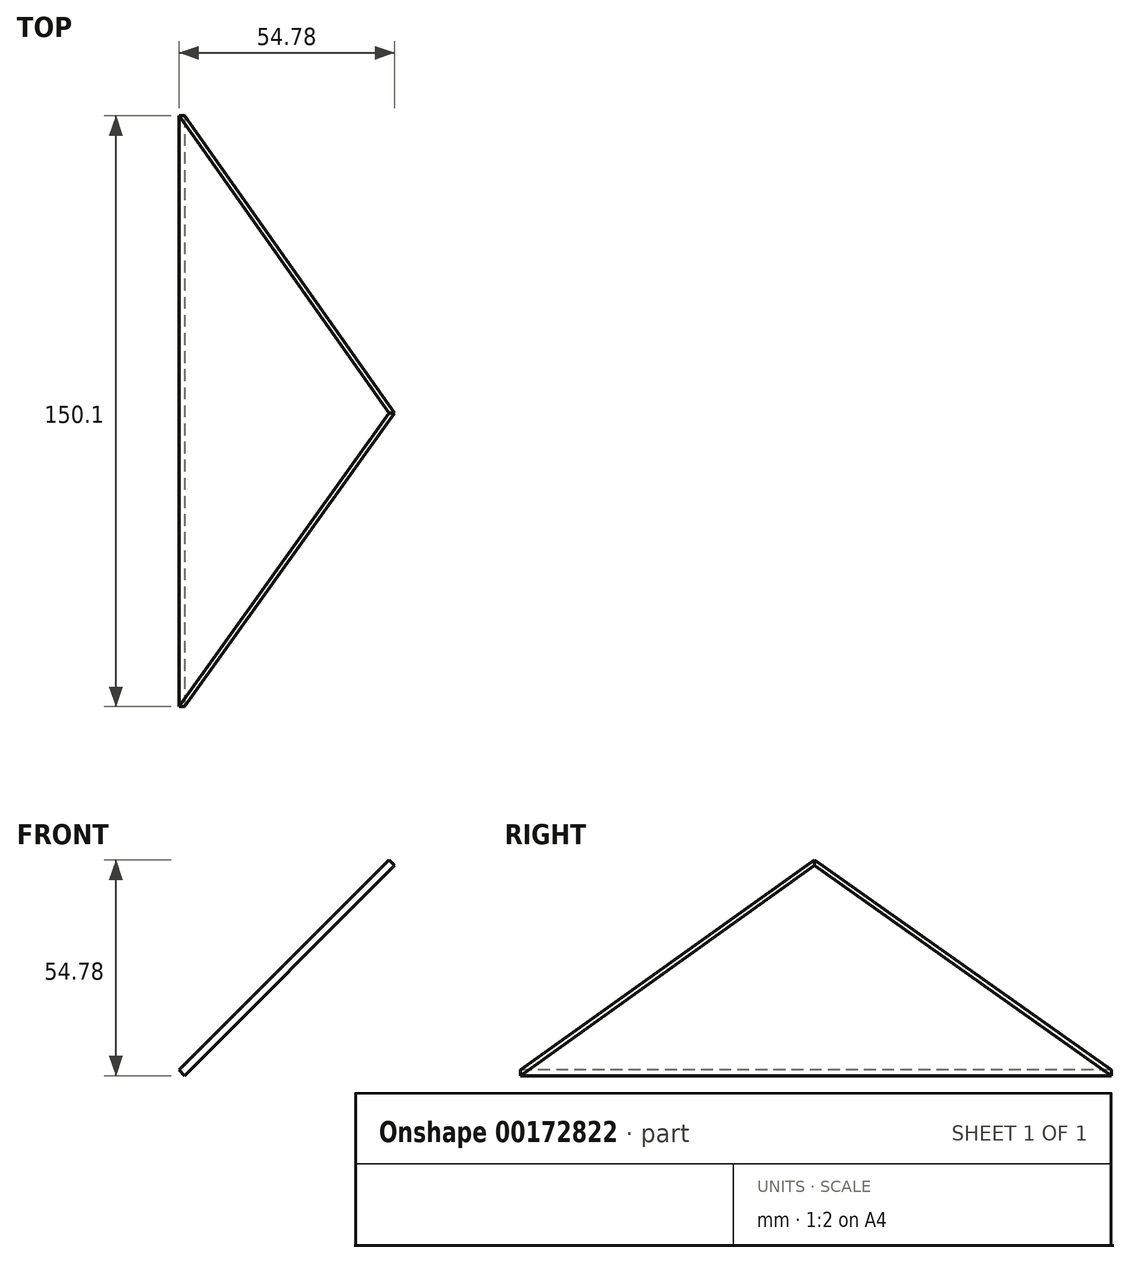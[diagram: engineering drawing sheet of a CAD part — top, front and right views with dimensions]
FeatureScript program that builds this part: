
annotation { "Feature Type Name" : "Feature", "Feature Type Description" : "" }
export const myFeature = defineFeature(function(context is Context, id is Id, definition is map)
    precondition{}
    {
        {
            var Q0;
            Q0=qCreatedBy(makeId("Top.planeOp"),FACE);
            var sketch = newSketch(context, id + "F0", { "sketchPlane" : qUnion([Q0])});
            skLineSegment(sketch, "E0.bottom", {"start": v(-75.48, 75.47) * mm, "end": v(75.05, 75.47) * mm});
            skLineSegment(sketch, "E0.top", {"start": v(-75.48, -74.63) * mm, "end": v(75.05, -74.63) * mm});
            skLineSegment(sketch, "E0.left", {"start": v(-75.48, 75.47) * mm, "end": v(-75.48, -74.63) * mm});
            skLineSegment(sketch, "E0.right", {"start": v(75.05, 75.47) * mm, "end": v(75.05, -74.63) * mm});
            skLineSegment(sketch, "E1", {"start": v(-75.48, -74.63) * mm, "end": v(0, 0) * mm});
            skLineSegment(sketch, "E2", {"start": v(0, 0) * mm, "end": v(75.05, 75.47) * mm});
            skLineSegment(sketch, "E3", {"start": v(-75.48, 75.47) * mm, "end": v(0, 0) * mm});
            skLineSegment(sketch, "E4", {"start": v(75.05, -74.63) * mm, "end": v(0, 0) * mm});
            skSolve(sketch);
        }
        {
            var Q0;
            Q0=qCreatedBy(makeId("Front.planeOp"),FACE);
            var sketch = newSketch(context, id + "F1", { "sketchPlane" : qUnion([Q0])});
            skPoint(sketch, "E5", {"position": v(0, 75.48) * mm});
            skLineSegment(sketch, "E6", {"start": v(0, 0) * mm, "end": v(0, 75.48) * mm, "construction": true});
            skLineSegment(sketch, "E7", {"start": v(-75.45, 0) * mm, "end": v(0, 75.48) * mm, "construction": true});
            skSolve(sketch);
        }
        {
            var Q0;
            Q0=makeQuery(id+"F0.imprint","IMPRINT",FACE,{"disambiguationData":[TD([[makeQuery(id+"F0.imprint","IMPRINT",EDGE,{"derivedFrom":sQuery(id+"F0.wireOp",EDGE,"E0.left")}),1.0]])]});
            var Q1;
            Q1=sQuery(id+"F0.wireOp",EDGE,"E3");
            var Q2;
            Q2=sQuery(id+"F0.wireOp",EDGE,"E0.left");
            var Q3;
            Q3=sQuery(id+"F0.wireOp",EDGE,"E1");
            extrude(context, id + "F2", {"entities" : qUnion([Q0]), "surfaceEntities" : qUnion([Q1, Q2, Q3]), "depth" : 2 * mm});
        }
        {
            var Q0;
            Q0=makeQuery(id+"F2.opExtrude","SWEPT_BODY",BODY,{"disambiguationData":[OSD([sQuery(id+"F0.wireOp",EDGE,"E0.left"),sQuery(id+"F0.wireOp",EDGE,"E1"),sQuery(id+"F0.wireOp",EDGE,"E3")])]});
            var Q1;
            Q1=sQuery(id+"F1.wireOp",VERTEX,"E5");
            var Q2;
            Q2=sQuery(id+"F1.wireOp",EDGE,"E7");
            var Q3;
            Q3=makeQuery(id+"F2.opExtrude","CAP_EDGE",EDGE,{"disambiguationData":[OSD([sQuery(id+"F0.wireOp",EDGE,"E0.left")])],"isStart":true});
            transform(context, id + "F3", {"entities" : qUnion([Q0]), "transformType" : TransformType.ROTATION, "transformAxis" : qUnion([Q3]), "angle" : 45 * degree, "makeCopy" : false});
        }
        {
            var Q0;
            Q0=makeQuery(id+"F2.opExtrude","SWEPT_BODY",BODY,{"disambiguationData":[OSD([sQuery(id+"F0.wireOp",EDGE,"E0.left"),sQuery(id+"F0.wireOp",EDGE,"E1"),sQuery(id+"F0.wireOp",EDGE,"E3")])]});
            var Q1;
            Q1=sQuery(id+"F1.wireOp",EDGE,"E7");
            var Q2;
            Q2=sQuery(id+"F1.wireOp",VERTEX,"E5");
            transform(context, id + "F4", {"entities" : qUnion([Q0]), "transformType" : TransformType.SCALE_UNIFORMLY, "scale" : 1, "scalePoint" : qUnion([Q2]), "makeCopy" : false});
        }
    });
